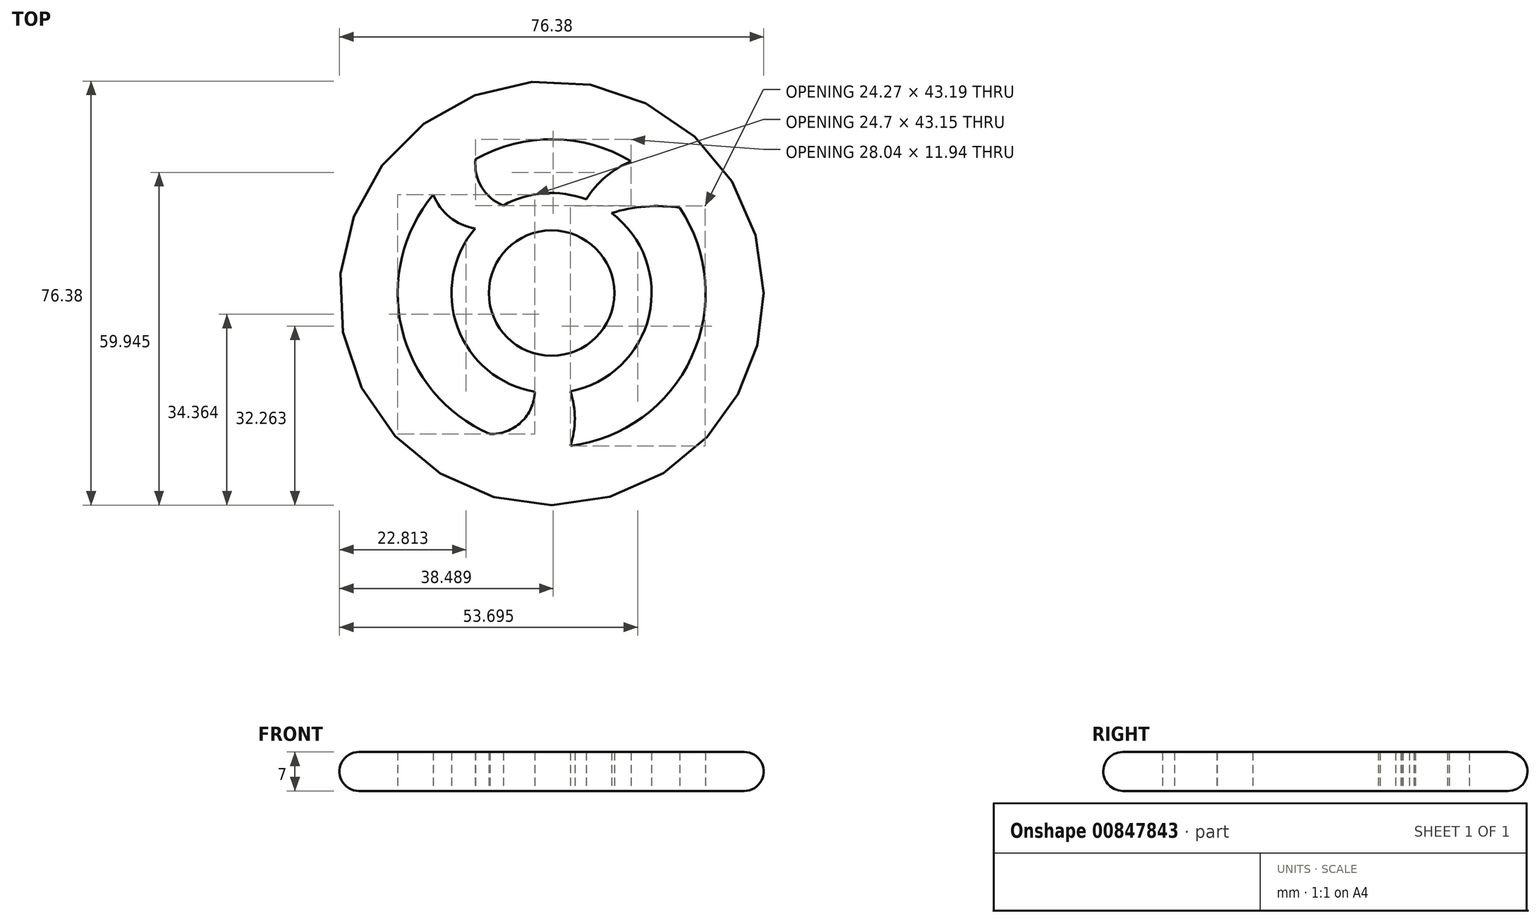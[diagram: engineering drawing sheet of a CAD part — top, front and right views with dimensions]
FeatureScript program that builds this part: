
annotation { "Feature Type Name" : "Feature", "Feature Type Description" : "" }
export const myFeature = defineFeature(function(context is Context, id is Id, definition is map)
    precondition{}
    {
        {
            var Q0;
            Q0=qCreatedBy(makeId("Top.planeOp"),FACE);
            var sketch = newSketch(context, id + "F0", { "sketchPlane" : qUnion([Q0])});
            skCircle(sketch, "E0", {"center": v(0, 0) * mm, "radius": 11.3 * mm});
            skCircle(sketch, "E1", {"center": v(0, 0) * mm, "radius": 38.2 * mm});
            skArc(sketch, "E2", {"start": v(3.37, -17.7) * mm, "mid": v(17.56, -4.07) * mm, "end": v(10.82, 14.41) * mm});
            skArc(sketch, "E3", {"start": v(3.37, -27.52) * mm, "mid": v(25.2, -11.57) * mm, "end": v(23.07, 15.37) * mm});
            skArc(sketch, "E4", {"start": v(-21.3, 17.75) * mm, "mid": v(-18.35, 13.69) * mm, "end": v(-13.76, 11.64) * mm});
            skArc(sketch, "E5", {"start": v(-13.67, 24.12) * mm, "mid": v(-12.6, 19.1) * mm, "end": v(-8.7, 15.79) * mm});
            skArc(sketch, "E6.trimOffspring", {"start": v(-21.3, 17.75) * mm, "mid": v(-26.98, -6.37) * mm, "end": v(-11.12, -25.4) * mm});
            skArc(sketch, "E7.trimOffspring", {"start": v(-13.76, 11.64) * mm, "mid": v(-16.93, -6.18) * mm, "end": v(-3.03, -17.77) * mm});
            skArc(sketch, "E8", {"start": v(14.32, 23.74) * mm, "mid": v(9.75, 20.95) * mm, "end": v(6.23, 16.91) * mm});
            skArc(sketch, "E9", {"start": v(23.07, 15.37) * mm, "mid": v(16.9, 15.6) * mm, "end": v(10.82, 14.41) * mm});
            skArc(sketch, "E10.trimOffspring", {"start": v(6.23, 16.91) * mm, "mid": v(-1.36, 17.97) * mm, "end": v(-8.7, 15.79) * mm});
            skArc(sketch, "E11.trimOffspring", {"start": v(14.32, 23.74) * mm, "mid": v(0.37, 27.72) * mm, "end": v(-13.67, 24.12) * mm});
            skArc(sketch, "E12", {"start": v(-11.12, -25.4) * mm, "mid": v(-5.5, -23.26) * mm, "end": v(-3.03, -17.77) * mm});
            skArc(sketch, "E13", {"start": v(3.37, -27.52) * mm, "mid": v(4.2, -22.61) * mm, "end": v(3.37, -17.7) * mm});
            skPoint(sketch, "E14.orphan", {"position": v(0, -27.73) * mm});
            skSolve(sketch);
        }
        {
            var Q0;
            Q0=makeQuery(id+"F0.imprint","IMPRINT",FACE,{"disambiguationData":[TD([[makeQuery(id+"F0.imprint","IMPRINT",EDGE,{"derivedFrom":sQuery(id+"F0.wireOp",EDGE,"E0")}),-1.0]])]});
            extrude(context, id + "F1", {"entities" : qUnion([Q0]), "depth" : 7 * mm, "offsetDistance" : 25 * mm});
        }
        {
            var Q0;
            Q0=makeQuery(id+"F1.opExtrude","CAP_EDGE",EDGE,{"disambiguationData":[OSD([sQuery(id+"F0.wireOp",EDGE,"E1")])],"isStart":false});
            var Q1;
            Q1=makeQuery(id+"F1.opExtrude","CAP_EDGE",EDGE,{"disambiguationData":[OSD([sQuery(id+"F0.wireOp",EDGE,"E1")])],"isStart":true});
            fillet(context, id + "F2", {"entities" : qUnion([Q0, Q1]), "radius" : 3.5 * mm, "tangentPropagation" : true, "allowEdgeOverflow" : false});
        }
    });
